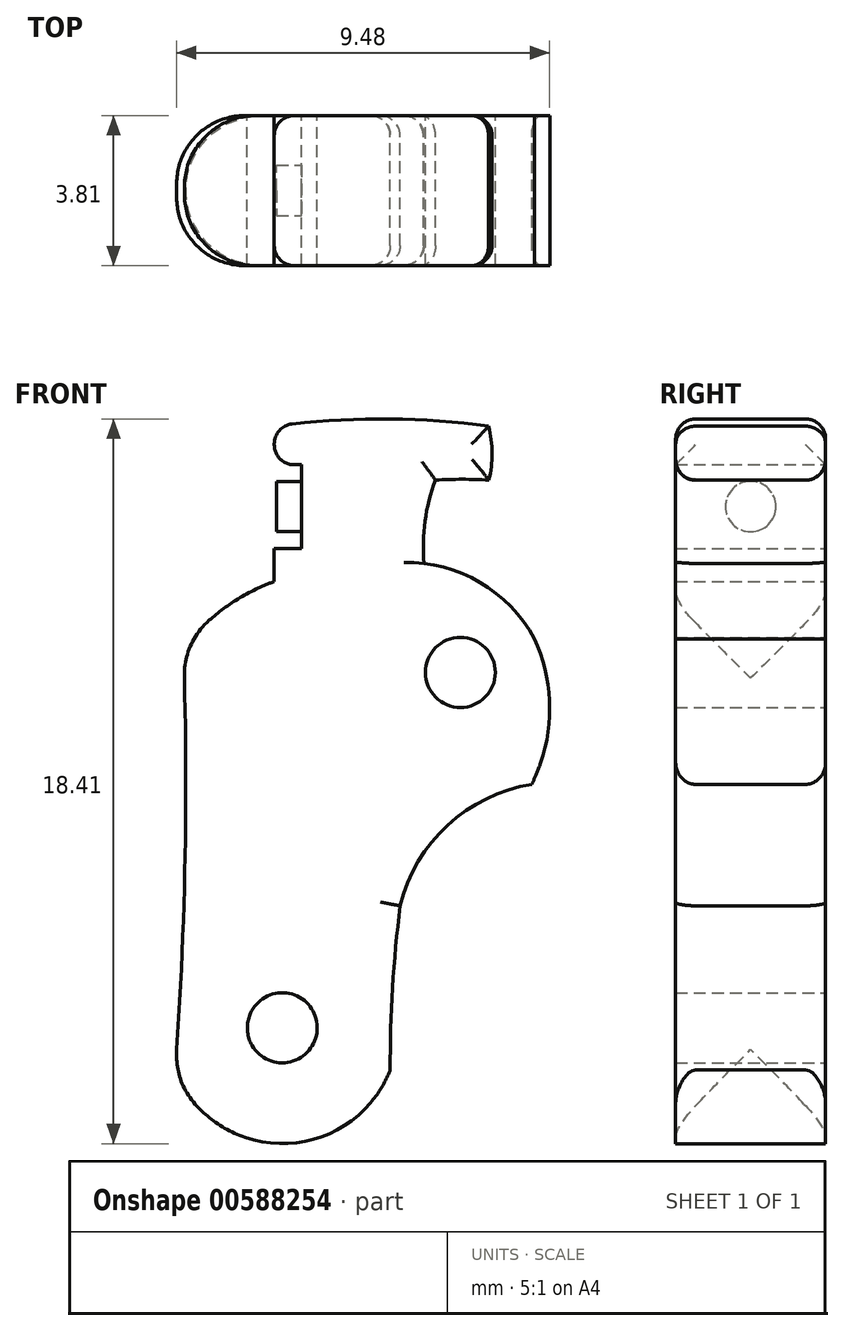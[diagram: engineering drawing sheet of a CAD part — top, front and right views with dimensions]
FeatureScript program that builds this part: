
annotation { "Feature Type Name" : "Feature", "Feature Type Description" : "" }
export const myFeature = defineFeature(function(context is Context, id is Id, definition is map)
    precondition{}
    {
        {
            var Q0;
            Q0=qCreatedBy(makeId("Front.planeOp"),FACE);
            var sketch = newSketch(context, id + "F0", { "sketchPlane" : qUnion([Q0])});
            skArc(sketch, "E0", {"start": v(-36.18, 30.57) * mm, "mid": v(-38.9, 30.75) * mm, "end": v(-41.63, 30.57) * mm});
            skArc(sketch, "E1", {"start": v(-35.02, 25.17) * mm, "mid": v(-36.19, 26.47) * mm, "end": v(-37.82, 27.08) * mm});
            skArc(sketch, "E2", {"start": v(-35.09, 21.47) * mm, "mid": v(-34.63, 23.31) * mm, "end": v(-35.02, 25.17) * mm});
            skPoint(sketch, "E3", {"position": v(-36.9, 24.31) * mm});
            skArc(sketch, "E4", {"start": v(-44.15, 14.16) * mm, "mid": v(-43.9, 19.54) * mm, "end": v(-43.94, 24.92) * mm});
            skArc(sketch, "E5", {"start": v(-35.09, 21.47) * mm, "mid": v(-37.22, 20.43) * mm, "end": v(-38.43, 18.38) * mm});
            skArc(sketch, "E6", {"start": v(-38.43, 18.38) * mm, "mid": v(-38.62, 16.3) * mm, "end": v(-38.68, 14.21) * mm});
            skArc(sketch, "E7", {"start": v(-44.15, 14.16) * mm, "mid": v(-41.4, 12.34) * mm, "end": v(-38.68, 14.21) * mm});
            skArc(sketch, "E8", {"start": v(-41.63, 26.62) * mm, "mid": v(-42.9, 25.94) * mm, "end": v(-43.94, 24.92) * mm});
            skLineSegment(sketch, "E9", {"start": v(-41.63, 30.57) * mm, "end": v(-41.63, 29.59) * mm});
            skLineSegment(sketch, "E10", {"start": v(-41.63, 29.59) * mm, "end": v(-40.93, 29.59) * mm});
            skLineSegment(sketch, "E11", {"start": v(-40.93, 29.59) * mm, "end": v(-40.93, 27.47) * mm});
            skLineSegment(sketch, "E12", {"start": v(-40.93, 27.47) * mm, "end": v(-41.63, 27.47) * mm});
            skLineSegment(sketch, "E13", {"start": v(-41.63, 27.47) * mm, "end": v(-41.63, 26.62) * mm});
            skArc(sketch, "E14", {"start": v(-37.53, 29.2) * mm, "mid": v(-37.8, 28.16) * mm, "end": v(-37.82, 27.08) * mm});
            skArc(sketch, "E15", {"start": v(-36.18, 29.2) * mm, "mid": v(-36.85, 29.22) * mm, "end": v(-37.53, 29.2) * mm});
            skArc(sketch, "E16", {"start": v(-36.18, 29.2) * mm, "mid": v(-36.1, 29.89) * mm, "end": v(-36.18, 30.57) * mm});
            skSolve(sketch);
        }
        {
            var Q0;
            Q0=makeQuery(id+"F0.imprint","IMPRINT",FACE,{"disambiguationData":[TD([[makeQuery(id+"F0.imprint","IMPRINT",EDGE,{"derivedFrom":sQuery(id+"F0.wireOp",EDGE,"OWMFxhSN-3WBP-GmBH-70HM-SY9r7lY3wJMt")}),1.0]])]});
            var Q1;
            Q1=makeQuery(id+"F0.imprint","IMPRINT",FACE,{"disambiguationData":[TD([[makeQuery(id+"F0.imprint","IMPRINT",EDGE,{"derivedFrom":sQuery(id+"F0.wireOp",EDGE,"E1")}),1.0]])]});
            extrude(context, id + "F1", {"entities" : qUnion([Q0, Q1]), "depth" : 3.8 * mm, "offsetDistance" : 25.4 * mm});
        }
        {
            var Q0;
            Q0=sQuery(id+"F0.wireOp",VERTEX,"dda5803d-23b6-492d-adbf-b0e8284d5be7");
            var Q1;
            Q1=sQuery(id+"F0.wireOp",VERTEX,"49b44927-d90c-40c4-b47c-8b709a41614f");
            var Q2;
            Q2=sQuery(id+"F0.wireOp",VERTEX,"E3");
            var Q3;
            Q3=makeQuery(id+"F1.opExtrude","SWEPT_BODY",BODY,{"disambiguationData":[OSD([sQuery(id+"F0.wireOp",EDGE,"OWMFxhSN-3WBP-GmBH-70HM-SY9r7lY3wJMt"),sQuery(id+"F0.wireOp",EDGE,"E0"),sQuery(id+"F0.wireOp",EDGE,"XJ3wd1zL-3AzV-Us8Q-e59q-DUijCpbfMa2Z"),sQuery(id+"F0.wireOp",EDGE,"0jgz9wQa-CzLe-zPMn-Q7Pv-oUmW80UOzPGC"),sQuery(id+"F0.wireOp",EDGE,"33xVBCY2-Zl1V-9e2d-plg4-WV1Z2fjrWSED"),sQuery(id+"F0.wireOp",EDGE,"rg2ucqn4-13Ef-ghLG-UZm5-3d3yGZTXAzio"),sQuery(id+"F0.wireOp",EDGE,"JC6zEkQU-rVTX-vbIi-Hnxb-VmMPNWEcaa7U"),sQuery(id+"F0.wireOp",EDGE,"Esrhtb8h-XGDk-EWN2-NKo5-URKT7jWZYait"),sQuery(id+"F0.wireOp",EDGE,"RUe499pp-jY0S-rKmp-wCeH-NheD3eOT8uJM")])]});
            hole(context, id + "F2", {"style" : HoleStyle.SIMPLE, "endStyle" : HoleEndStyle.THROUGH, "oppositeDirection" : true, "holeDiameter" : 1.78 * mm, "majorDiameter" : 6.35 * mm, "isTappedThrough" : true, "tappedDepth" : 12.7 * mm, "tapClearance" : 3, "locations" : qUnion([Q0, Q1, Q2]), "scope" : qUnion([Q3])});
        }
        {
            var Q0;
            Q0=makeQuery(id+"F1.opExtrude","CAP_EDGE",EDGE,{"disambiguationData":[OSD([sQuery(id+"F0.wireOp",EDGE,"E15")])],"isStart":false});
            var Q1;
            Q1=makeQuery(id+"F1.opExtrude","CAP_EDGE",EDGE,{"disambiguationData":[OSD([sQuery(id+"F0.wireOp",EDGE,"E16")])],"isStart":false});
            var Q2;
            Q2=makeQuery(id+"F1.opExtrude","CAP_EDGE",EDGE,{"disambiguationData":[OSD([sQuery(id+"F0.wireOp",EDGE,"E14")])],"isStart":false});
            var Q3;
            Q3=makeQuery(id+"F1.opExtrude","CAP_EDGE",EDGE,{"disambiguationData":[OSD([sQuery(id+"F0.wireOp",EDGE,"E14")])],"isStart":true});
            var Q4;
            Q4=makeQuery(id+"F1.opExtrude","CAP_EDGE",EDGE,{"disambiguationData":[OSD([sQuery(id+"F0.wireOp",EDGE,"E15")])],"isStart":true});
            var Q5;
            Q5=makeQuery(id+"F1.opExtrude","CAP_EDGE",EDGE,{"disambiguationData":[OSD([sQuery(id+"F0.wireOp",EDGE,"E0")])],"isStart":true});
            var Q6;
            Q6=makeQuery(id+"F1.opExtrude","CAP_EDGE",EDGE,{"disambiguationData":[OSD([sQuery(id+"F0.wireOp",EDGE,"E16")])],"isStart":true});
            var Q7;
            Q7=makeQuery(id+"F1.opExtrude","CAP_EDGE",EDGE,{"disambiguationData":[OSD([sQuery(id+"F0.wireOp",EDGE,"E0")])],"isStart":false});
            var Q8;
            Q8=makeQuery(id+"F1.opExtrude","SWEPT_EDGE",EDGE,{"disambiguationData":[OSD([sQuery(id+"F0.wireOp",EDGE,"E0"),sQuery(id+"F0.wireOp",EDGE,"E9")])]});
            var Q9;
            Q9=makeQuery(id+"F1.opExtrude","SWEPT_FACE",FACE,{"disambiguationData":[OSD([sQuery(id+"F0.wireOp",EDGE,"E9")])]});
            var Q10;
            Q10=makeQuery(id+"F1.opExtrude","CAP_EDGE",EDGE,{"disambiguationData":[OSD([sQuery(id+"F0.wireOp",EDGE,"E5")])],"isStart":false});
            var Q11;
            Q11=makeQuery(id+"F1.opExtrude","CAP_EDGE",EDGE,{"disambiguationData":[OSD([sQuery(id+"F0.wireOp",EDGE,"E6")])],"isStart":false});
            var Q12;
            Q12=makeQuery(id+"F1.opExtrude","CAP_EDGE",EDGE,{"disambiguationData":[OSD([sQuery(id+"F0.wireOp",EDGE,"E5")])],"isStart":true});
            var Q13;
            Q13=makeQuery(id+"F1.opExtrude","CAP_EDGE",EDGE,{"disambiguationData":[OSD([sQuery(id+"F0.wireOp",EDGE,"E6")])],"isStart":true});
            fillet(context, id + "F3", {"entities" : qUnion([Q0, Q1, Q2, Q3, Q4, Q5, Q6, Q7, Q8, Q9, Q10, Q11, Q12, Q13]), "radius" : 0.5 * mm, "tangentPropagation" : true, "allowEdgeOverflow" : false});
        }
        {
            var Q0;
            Q0=sQuery(id+"F0.wireOp",VERTEX,"E7.center");
            var Q1;
            Q1=makeQuery(id+"F1.opExtrude","SWEPT_BODY",BODY,{"disambiguationData":[OSD([sQuery(id+"F0.wireOp",EDGE,"OWMFxhSN-3WBP-GmBH-70HM-SY9r7lY3wJMt"),sQuery(id+"F0.wireOp",EDGE,"E0"),sQuery(id+"F0.wireOp",EDGE,"XJ3wd1zL-3AzV-Us8Q-e59q-DUijCpbfMa2Z"),sQuery(id+"F0.wireOp",EDGE,"0jgz9wQa-CzLe-zPMn-Q7Pv-oUmW80UOzPGC"),sQuery(id+"F0.wireOp",EDGE,"rg2ucqn4-13Ef-ghLG-UZm5-3d3yGZTXAzio"),sQuery(id+"F0.wireOp",EDGE,"E1"),sQuery(id+"F0.wireOp",EDGE,"E2"),sQuery(id+"F0.wireOp",EDGE,"E4"),sQuery(id+"F0.wireOp",EDGE,"E5"),sQuery(id+"F0.wireOp",EDGE,"E6"),sQuery(id+"F0.wireOp",EDGE,"E7")])]});
            hole(context, id + "F4", {"style" : HoleStyle.SIMPLE, "endStyle" : HoleEndStyle.THROUGH, "oppositeDirection" : true, "holeDiameter" : 1.78 * mm, "majorDiameter" : 6.35 * mm, "isTappedThrough" : true, "tappedDepth" : 12.7 * mm, "tapClearance" : 3, "locations" : qUnion([Q0]), "scope" : qUnion([Q1])});
        }
        {
            var Q0;
            Q0=makeQuery(id+"F1.opExtrude","SWEPT_FACE",FACE,{"disambiguationData":[OSD([sQuery(id+"F0.wireOp",EDGE,"E4")])]});
            fillet(context, id + "F5", {"entities" : qUnion([Q0]), "radius" : 1.9 * mm, "tangentPropagation" : true, "allowEdgeOverflow" : false});
        }
        {
            var Q0;
            Q0=makeQuery(id+"F1.opExtrude","SWEPT_FACE",FACE,{"disambiguationData":[OSD([sQuery(id+"F0.wireOp",EDGE,"E11")])]});
            var sketch = newSketch(context, id + "F6", { "sketchPlane" : qUnion([Q0])});
            skCircle(sketch, "E17", {"center": v(1.9, 28.53) * mm, "radius": 0.64 * mm});
            skPoint(sketch, "E17.centerSnap0", {"position": v(3.81, 28.53) * mm});
            skPoint(sketch, "E17.centerSnap1", {"position": v(1.9, 27.47) * mm});
            skSolve(sketch);
        }
        {
            var Q0;
            Q0=makeQuery(id+"F6.imprint","IMPRINT",FACE,{"disambiguationData":[TD([[makeQuery(id+"F6.imprint","IMPRINT",EDGE,{"derivedFrom":sQuery(id+"F6.wireOp",EDGE,"E17")}),1.0]])]});
            extrude(context, id + "F7", {"entities" : qUnion([Q0]), "operationType" : NewBodyOperationType.ADD, "depth" : 0.63 * mm, "offsetDistance" : 25.4 * mm});
        }
    });
